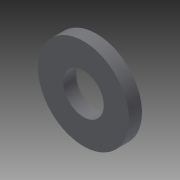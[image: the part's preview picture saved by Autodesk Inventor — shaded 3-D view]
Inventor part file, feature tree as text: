
AUTODESK INVENTOR PART (.ipt)
format: ipt  version: 2014 (Build 180170000, 170)  size: 102,400 bytes
history: native  units: in
note: dims shown in document units (in); Inventor stores cm internally (conversion verified against a paired STEP export)
features: other x7, revolve x1, sketch x1
ambient origin geometry x8: Origin, YZ Plane, XZ Plane, XY Plane, X Axis, Y Axis, Z Axis, Center Point
bodies: Solid1 (feature_tree)
feature tree (9):
  revolve  "Revolution1"  [1 undecoded]
  other  "part_to_rod_XY"
  other  "part_to_rod_YZ"
  other  "part_to_rod_ZX"
  other  "part_to_rod_X"
  other  "part_to_rod_Y"
  other  "part_to_rod_Z"
  other  "part_to_rod_Center"
  sketch  "Sketch_1"  dims[d0=360.0deg]
note: 1 required parameter value undecoded (feature->parameter linkage not recoverable at this tier; creation-order binding heuristic only, values carry confidence <= 0.55)
